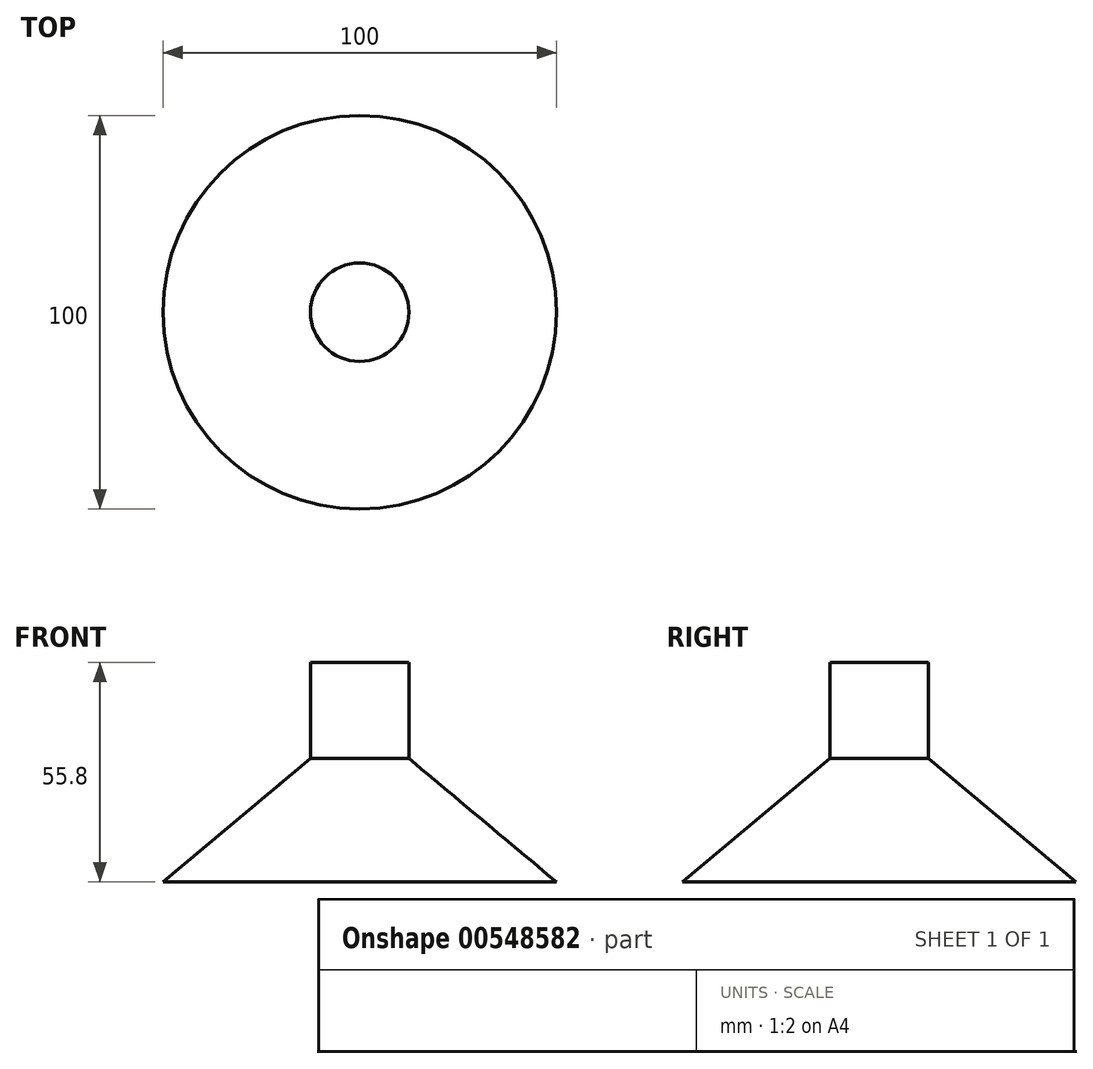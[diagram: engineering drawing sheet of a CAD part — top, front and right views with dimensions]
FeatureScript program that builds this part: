
annotation { "Feature Type Name" : "Feature", "Feature Type Description" : "" }
export const myFeature = defineFeature(function(context is Context, id is Id, definition is map)
    precondition{}
    {
        {
            var Q0;
            Q0=qCreatedBy(makeId("Top.planeOp"),FACE);
            var sketch = newSketch(context, id + "F0", { "sketchPlane" : qUnion([Q0])});
            skCircle(sketch, "E0", {"center": v(0, 0) * mm, "radius": 50 * mm});
            skSolve(sketch);
        }
        {
            var Q0;
            Q0=qCreatedBy(makeId("Top.planeOp"),FACE);
            cPlane(context, id + "F1", {"entities" : qUnion([Q0]), "cplaneType" : CPlaneType.OFFSET, "offset" : 31.4 * mm, "width" : 150 * mm, "height" : 150 * mm});
        }
        {
            var Q0;
            Q0=qCreatedBy(id+"F1.planeOp",FACE);
            var sketch = newSketch(context, id + "F2", { "sketchPlane" : qUnion([Q0])});
            skCircle(sketch, "E1", {"center": v(0, 0) * mm, "radius": 12.5 * mm});
            skSolve(sketch);
        }
        {
            var Q0;
            Q0=qCreatedBy(id+"F1.planeOp",FACE);
            cPlane(context, id + "F3", {"entities" : qUnion([Q0]), "cplaneType" : CPlaneType.OFFSET, "offset" : 24.4 * mm, "width" : 150 * mm, "height" : 150 * mm});
        }
        {
            var Q0;
            Q0=makeQuery(id+"F2.imprint","IMPRINT",FACE,{"disambiguationData":[TD([[makeQuery(id+"F2.imprint","IMPRINT",EDGE,{"derivedFrom":sQuery(id+"F2.wireOp",EDGE,"E1")}),1.0]])]});
            var Q1;
            Q1=makeQuery(id+"F0.imprint","IMPRINT",FACE,{"disambiguationData":[TD([[makeQuery(id+"F0.imprint","IMPRINT",EDGE,{"derivedFrom":sQuery(id+"F0.wireOp",EDGE,"E0")}),1.0]])]});
            loft(context, id + "F4", {"sheetProfilesArray" : [{ "sheetProfileEntities" : qUnion([Q0]) }, { "sheetProfileEntities" : qUnion([Q1]) }]});
        }
        {
            var Q0;
            Q0=qCreatedBy(id+"F3.planeOp",FACE);
            var sketch = newSketch(context, id + "F5", { "sketchPlane" : qUnion([Q0])});
            skCircle(sketch, "E2", {"center": v(0, 0) * mm, "radius": 12.5 * mm});
            skSolve(sketch);
        }
        {
            var Q1;
            Q1=makeQuery(id+"F5.imprint","IMPRINT",FACE,{"disambiguationData":[TD([[makeQuery(id+"F5.imprint","IMPRINT",EDGE,{"derivedFrom":sQuery(id+"F5.wireOp",EDGE,"E2")}),1.0]])]});
            var Q2;
            Q2=makeQuery(id+"F4.opLoft","CAP_FACE",FACE,{"disambiguationData":[OSD([makeQuery(id+"F2.imprint","IMPRINT",FACE,{"disambiguationData":[TD([[makeQuery(id+"F2.imprint","IMPRINT",EDGE,{"derivedFrom":sQuery(id+"F2.wireOp",EDGE,"E1")}),1.0]])]})])],"isStart":true});
            loft(context, id + "F6", {"operationType" : NewBodyOperationType.ADD, "sheetProfilesArray" : [{ "sheetProfileEntities" : qUnion([Q1]) }, { "sheetProfileEntities" : qUnion([Q2]) }]});
        }
    });
